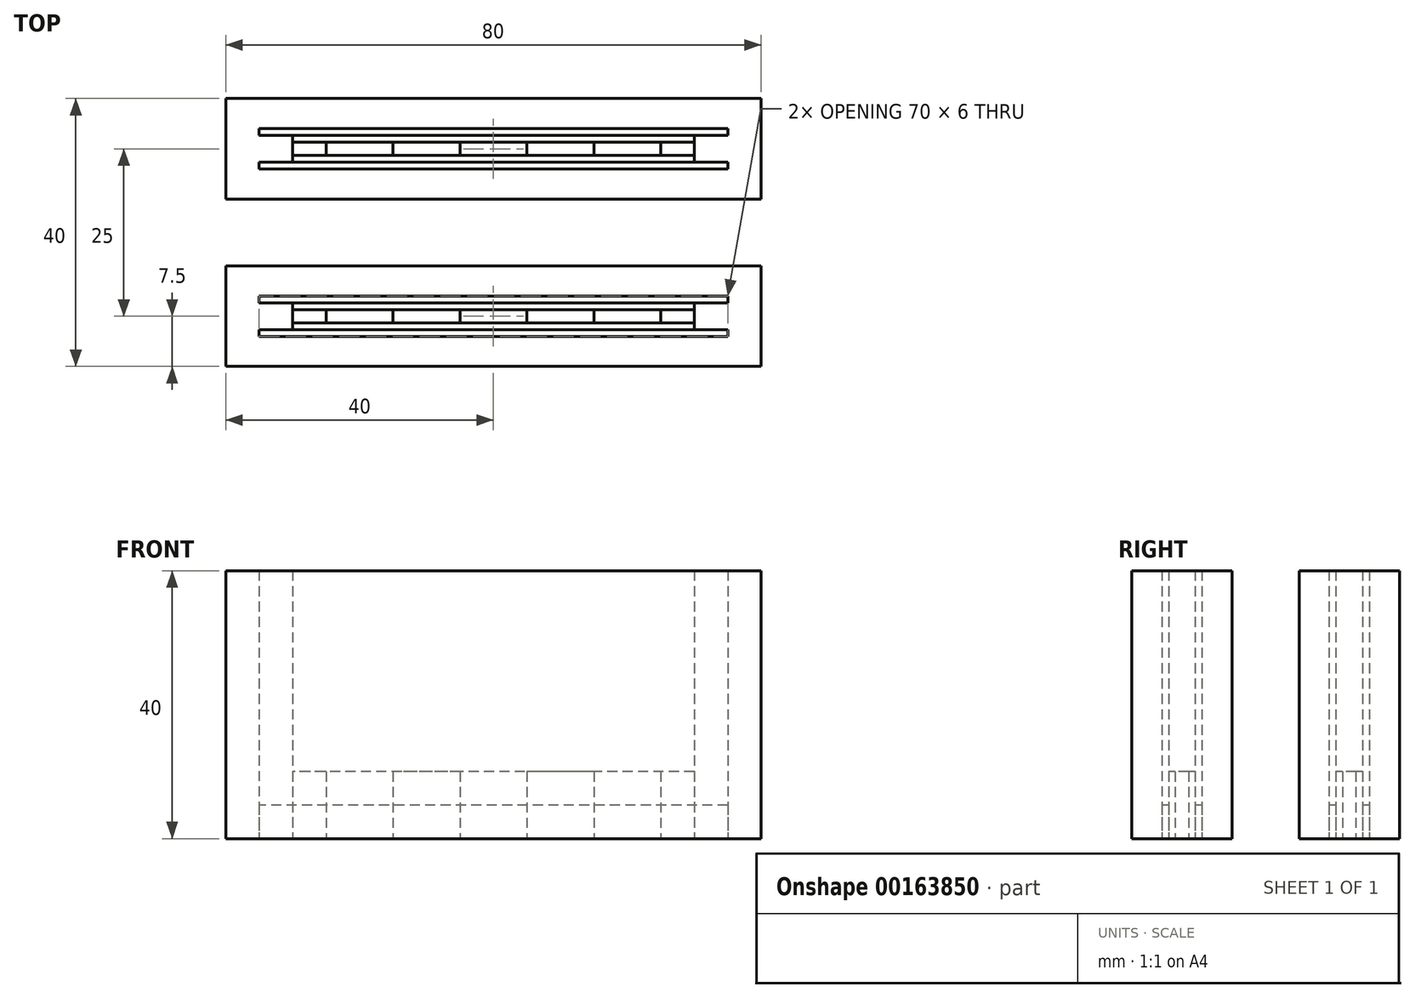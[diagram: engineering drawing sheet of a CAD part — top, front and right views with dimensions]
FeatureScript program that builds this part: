
annotation { "Feature Type Name" : "Feature", "Feature Type Description" : "" }
export const myFeature = defineFeature(function(context is Context, id is Id, definition is map)
    precondition{}
    {
        {
            var Q0;
            Q0=qCreatedBy(makeId("Top.planeOp"),FACE);
            var sketch = newSketch(context, id + "F0", { "sketchPlane" : qUnion([Q0])});
            skLineSegment(sketch, "E0.bottom", {"start": v(40, 7.5) * mm, "end": v(-40, 7.5) * mm});
            skLineSegment(sketch, "E0.top", {"start": v(40, -7.5) * mm, "end": v(-40, -7.5) * mm});
            skLineSegment(sketch, "E0.left", {"start": v(40, 7.5) * mm, "end": v(40, -7.5) * mm});
            skLineSegment(sketch, "E0.right", {"start": v(-40, 7.5) * mm, "end": v(-40, -7.5) * mm});
            skPoint(sketch, "E0.middle", {"position": v(0, 0) * mm});
            skLineSegment(sketch, "E1.0", {"start": v(35, 3) * mm, "end": v(-35, 3) * mm});
            skLineSegment(sketch, "E2.0", {"start": v(35, -3) * mm, "end": v(-35, -3) * mm});
            skLineSegment(sketch, "E3.0", {"start": v(35, -2) * mm, "end": v(-35, -2) * mm});
            skLineSegment(sketch, "E4.0", {"start": v(35, 2) * mm, "end": v(-35, 2) * mm});
            skLineSegment(sketch, "E5.0", {"start": v(30, -1) * mm, "end": v(-30, -1) * mm});
            skLineSegment(sketch, "E6.0", {"start": v(30, 1) * mm, "end": v(-30, 1) * mm});
            skLineSegment(sketch, "E7.0", {"start": v(35, 3) * mm, "end": v(35, 2) * mm});
            skLineSegment(sketch, "E8.0", {"start": v(30, 2) * mm, "end": v(30, -2) * mm});
            skLineSegment(sketch, "E9.0", {"start": v(25, 1) * mm, "end": v(25, -1) * mm});
            skLineSegment(sketch, "E10.0", {"start": v(15, 1) * mm, "end": v(15, -1) * mm});
            skLineSegment(sketch, "E11.0", {"start": v(5, 1) * mm, "end": v(5, -1) * mm});
            skLineSegment(sketch, "E12.0", {"start": v(-35, 3) * mm, "end": v(-35, 2) * mm});
            skLineSegment(sketch, "E13.0", {"start": v(-30, 2) * mm, "end": v(-30, -2) * mm});
            skLineSegment(sketch, "E14.0", {"start": v(-5, 1) * mm, "end": v(-5, -1) * mm});
            skLineSegment(sketch, "E15.0", {"start": v(-15, 1) * mm, "end": v(-15, -1) * mm});
            skLineSegment(sketch, "E16.0", {"start": v(-25, 1) * mm, "end": v(-25, -1) * mm});
            skLineSegment(sketch, "E17.0.1.0", {"start": v(35, 28) * mm, "end": v(-35, 28) * mm});
            skLineSegment(sketch, "E17.0.1.1", {"start": v(35, 23) * mm, "end": v(-35, 23) * mm});
            skLineSegment(sketch, "E17.0.1.2", {"start": v(40, 32.5) * mm, "end": v(40, 17.5) * mm});
            skLineSegment(sketch, "E17.0.1.3", {"start": v(30, 26) * mm, "end": v(-30, 26) * mm});
            skLineSegment(sketch, "E17.0.1.4", {"start": v(40, 17.5) * mm, "end": v(-40, 17.5) * mm});
            skPoint(sketch, "E17.0.1.5", {"position": v(0, 25) * mm});
            skLineSegment(sketch, "E17.0.1.6", {"start": v(-40, 32.5) * mm, "end": v(-40, 17.5) * mm});
            skLineSegment(sketch, "E17.0.1.7", {"start": v(35, 22) * mm, "end": v(-35, 22) * mm});
            skLineSegment(sketch, "E17.0.1.8", {"start": v(40, 32.5) * mm, "end": v(-40, 32.5) * mm});
            skLineSegment(sketch, "E17.0.1.9", {"start": v(35, 27) * mm, "end": v(-35, 27) * mm});
            skLineSegment(sketch, "E17.0.1.10", {"start": v(30, 24) * mm, "end": v(-30, 24) * mm});
            skLineSegment(sketch, "E17.0.1.11", {"start": v(-25, 26) * mm, "end": v(-25, 24) * mm});
            skLineSegment(sketch, "E17.0.1.12", {"start": v(-5, 26) * mm, "end": v(-5, 24) * mm});
            skLineSegment(sketch, "E17.0.1.13", {"start": v(15, 26) * mm, "end": v(15, 24) * mm});
            skLineSegment(sketch, "E17.0.1.14", {"start": v(5, 26) * mm, "end": v(5, 24) * mm});
            skLineSegment(sketch, "E17.0.1.15", {"start": v(-35, 28) * mm, "end": v(-35, 27) * mm});
            skLineSegment(sketch, "E17.0.1.16", {"start": v(-15, 26) * mm, "end": v(-15, 24) * mm});
            skLineSegment(sketch, "E17.0.1.17", {"start": v(35, 28) * mm, "end": v(35, 27) * mm});
            skLineSegment(sketch, "E17.0.1.18", {"start": v(30, 27) * mm, "end": v(30, 23) * mm});
            skLineSegment(sketch, "E17.0.1.19", {"start": v(25, 26) * mm, "end": v(25, 24) * mm});
            skLineSegment(sketch, "E17.0.1.20", {"start": v(-30, 27) * mm, "end": v(-30, 23) * mm});
            skLineSegment(sketch, "E17.direction1", {"start": v(-40, -7.5) * mm, "end": v(-15, -7.5) * mm, "construction": true});
            skLineSegment(sketch, "E17.direction2", {"start": v(-40, -7.5) * mm, "end": v(-40, 17.5) * mm, "construction": true});
            skLineSegment(sketch, "E18.trimOffspring", {"start": v(-35, -2) * mm, "end": v(-35, -3) * mm});
            skLineSegment(sketch, "E19.trimOffspring", {"start": v(35, -2) * mm, "end": v(35, -3) * mm});
            skLineSegment(sketch, "E20.trimOffspring", {"start": v(35, 23) * mm, "end": v(35, 22) * mm});
            skLineSegment(sketch, "E21.trimOffspring", {"start": v(-35, 23) * mm, "end": v(-35, 22) * mm});
            skSolve(sketch);
        }
        {
            var Q0;
            Q0=makeQuery(id+"F0.imprint","IMPRINT",FACE,{"disambiguationData":[TD([[makeQuery(id+"F0.imprint","IMPRINT",EDGE,{"derivedFrom":sQuery(id+"F0.wireOp",EDGE,"E0.bottom")}),1.0]])]});
            var Q1;
            Q1=makeQuery(id+"F0.imprint","IMPRINT",FACE,{"disambiguationData":[TD([[makeQuery(id+"F0.imprint","IMPRINT",EDGE,{"derivedFrom":sQuery(id+"F0.wireOp",EDGE,"E17.0.1.0")}),-1.0]])]});
            extrude(context, id + "F1", {"entities" : qUnion([Q0, Q1]), "depth" : 40 * mm});
        }
        {
            var Q0;
            Q0=makeQuery(id+"F0.imprint","IMPRINT",FACE,{"disambiguationData":[TD([[makeQuery(id+"F0.imprint","IMPRINT",EDGE,{"derivedFrom":sQuery(id+"F0.wireOp",EDGE,"E17.0.1.7")}),-1.0]])]});
            var Q1;
            Q1=makeQuery(id+"F0.imprint","IMPRINT",FACE,{"disambiguationData":[TD([[makeQuery(id+"F0.imprint","IMPRINT",EDGE,{"derivedFrom":sQuery(id+"F0.wireOp",EDGE,"E17.0.1.0")}),1.0]])]});
            var Q2;
            Q2=makeQuery(id+"F0.imprint","IMPRINT",FACE,{"disambiguationData":[TD([[makeQuery(id+"F0.imprint","IMPRINT",EDGE,{"derivedFrom":sQuery(id+"F0.wireOp",EDGE,"E1.0")}),1.0]])]});
            var Q3;
            Q3=makeQuery(id+"F0.imprint","IMPRINT",FACE,{"disambiguationData":[TD([[makeQuery(id+"F0.imprint","IMPRINT",EDGE,{"derivedFrom":sQuery(id+"F0.wireOp",EDGE,"E2.0")}),-1.0]])]});
            extrude(context, id + "F2", {"entities" : qUnion([Q0, Q1, Q2, Q3]), "depth" : 5 * mm});
        }
        {
            var Q0;
            {var subQ4=sQuery(id+"F0.wireOp",EDGE,"E8.0");var subQ6=sQuery(id+"F0.wireOp",EDGE,"E4.0");var subQ7=makeQuery(id+"F0.imprint","INTERSECT",VERTEX,{"derivedFrom":[subQ6,subQ4]});Q0=makeQuery(id+"F0.imprint","IMPRINT",FACE,{"disambiguationData":[TD([[makeQuery(id+"F0.imprint","IMPRINT",EDGE,{"disambiguationData":[TD([[subQ7,-1.0]])],"derivedFrom":subQ6}),1.0]])]});}
            var Q1;
            {var subQ3=sQuery(id+"F0.wireOp",EDGE,"E8.0");var subQ4=sQuery(id+"F0.wireOp",EDGE,"E3.0");var subQ5=makeQuery(id+"F0.imprint","INTERSECT",VERTEX,{"derivedFrom":[subQ4,subQ3]});Q1=makeQuery(id+"F0.imprint","IMPRINT",FACE,{"disambiguationData":[TD([[makeQuery(id+"F0.imprint","IMPRINT",EDGE,{"disambiguationData":[TD([[subQ5,-1.0]])],"derivedFrom":subQ4}),-1.0]])]});}
            var Q2;
            {var subQ4=sQuery(id+"F0.wireOp",EDGE,"E17.0.1.18");var subQ6=sQuery(id+"F0.wireOp",EDGE,"E17.0.1.1");var subQ7=makeQuery(id+"F0.imprint","INTERSECT",VERTEX,{"derivedFrom":[subQ6,subQ4]});Q2=makeQuery(id+"F0.imprint","IMPRINT",FACE,{"disambiguationData":[TD([[makeQuery(id+"F0.imprint","IMPRINT",EDGE,{"disambiguationData":[TD([[subQ7,-1.0]])],"derivedFrom":subQ6}),-1.0]])]});}
            var Q3;
            {var subQ0=sQuery(id+"F0.wireOp",EDGE,"E17.0.1.3");var subQ9=sQuery(id+"F0.wireOp",EDGE,"E17.0.1.18");var subQ10=makeQuery(id+"F0.imprint","INTERSECT",VERTEX,{"derivedFrom":[subQ0,subQ9]});Q3=makeQuery(id+"F0.imprint","IMPRINT",FACE,{"disambiguationData":[TD([[makeQuery(id+"F0.imprint","IMPRINT",EDGE,{"disambiguationData":[TD([[subQ10,-1.0]])],"derivedFrom":subQ0}),-1.0]])]});}
            extrude(context, id + "F3", {"entities" : qUnion([Q0, Q1, Q2, Q3]), "depth" : 10 * mm});
        }
        {
            var Q0;
            {var subQ3=sQuery(id+"F0.wireOp",EDGE,"E17.0.1.19");Q0=makeQuery(id+"F0.imprint","IMPRINT",FACE,{"disambiguationData":[TD([[makeQuery(id+"F0.imprint","IMPRINT",EDGE,{"derivedFrom":subQ3}),1.0]])]});}
            var Q1;
            {var subQ0=sQuery(id+"F0.wireOp",EDGE,"E17.0.1.13");Q1=makeQuery(id+"F0.imprint","IMPRINT",FACE,{"disambiguationData":[TD([[makeQuery(id+"F0.imprint","IMPRINT",EDGE,{"derivedFrom":subQ0}),-1.0]])]});}
            var Q2;
            {var subQ0=sQuery(id+"F0.wireOp",EDGE,"E17.0.1.12");Q2=makeQuery(id+"F0.imprint","IMPRINT",FACE,{"disambiguationData":[TD([[makeQuery(id+"F0.imprint","IMPRINT",EDGE,{"derivedFrom":subQ0}),-1.0]])]});}
            var Q3;
            {var subQ3=sQuery(id+"F0.wireOp",EDGE,"E17.0.1.11");Q3=makeQuery(id+"F0.imprint","IMPRINT",FACE,{"disambiguationData":[TD([[makeQuery(id+"F0.imprint","IMPRINT",EDGE,{"derivedFrom":subQ3}),-1.0]])]});}
            var Q4;
            {var subQ3=sQuery(id+"F0.wireOp",EDGE,"E9.0");Q4=makeQuery(id+"F0.imprint","IMPRINT",FACE,{"disambiguationData":[TD([[makeQuery(id+"F0.imprint","IMPRINT",EDGE,{"derivedFrom":subQ3}),1.0]])]});}
            var Q5;
            {var subQ0=sQuery(id+"F0.wireOp",EDGE,"E10.0");Q5=makeQuery(id+"F0.imprint","IMPRINT",FACE,{"disambiguationData":[TD([[makeQuery(id+"F0.imprint","IMPRINT",EDGE,{"derivedFrom":subQ0}),-1.0]])]});}
            var Q6;
            {var subQ0=sQuery(id+"F0.wireOp",EDGE,"E14.0");Q6=makeQuery(id+"F0.imprint","IMPRINT",FACE,{"disambiguationData":[TD([[makeQuery(id+"F0.imprint","IMPRINT",EDGE,{"derivedFrom":subQ0}),-1.0]])]});}
            var Q7;
            {var subQ3=sQuery(id+"F0.wireOp",EDGE,"E16.0");Q7=makeQuery(id+"F0.imprint","IMPRINT",FACE,{"disambiguationData":[TD([[makeQuery(id+"F0.imprint","IMPRINT",EDGE,{"derivedFrom":subQ3}),-1.0]])]});}
            extrude(context, id + "F4", {"entities" : qUnion([Q0, Q1, Q2, Q3, Q4, Q5, Q6, Q7]), "depth" : 10 * mm});
        }
    });
